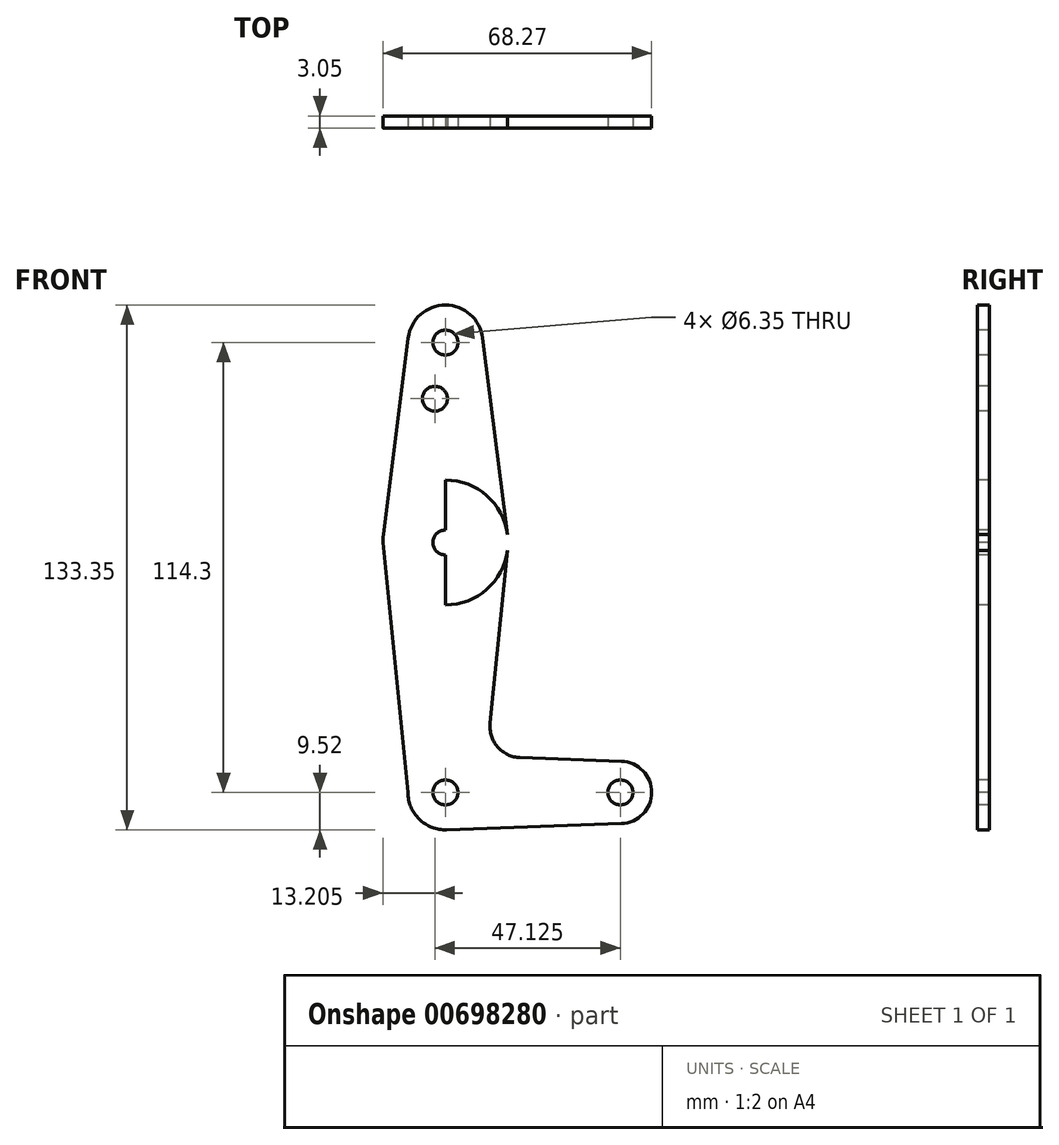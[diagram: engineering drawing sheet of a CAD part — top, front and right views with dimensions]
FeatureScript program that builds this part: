
annotation { "Feature Type Name" : "Feature", "Feature Type Description" : "" }
export const myFeature = defineFeature(function(context is Context, id is Id, definition is map)
    precondition{}
    {
        {
            var Q0;
            Q0=qCreatedBy(makeId("Front.planeOp"),FACE);
            var sketch = newSketch(context, id + "F0", { "sketchPlane" : qUnion([Q0])});
            skLineSegment(sketch, "E0", {"start": v(0, 114.3) * mm, "end": v(0, 0) * mm});
            skLineSegment(sketch, "E1", {"start": v(44.45, 0) * mm, "end": v(0, 0) * mm});
            skCircle(sketch, "E2", {"center": v(0, 114.3) * mm, "radius": 9.53 * mm});
            skCircle(sketch, "E3", {"center": v(0, 0) * mm, "radius": 9.53 * mm});
            skCircle(sketch, "E4", {"center": v(44.45, 0) * mm, "radius": 7.94 * mm});
            skCircle(sketch, "E5", {"center": v(0, 63.5) * mm, "radius": 15.88 * mm});
            skLineSegment(sketch, "E6", {"start": v(-9.45, 115.5) * mm, "end": v(-15.75, 65.48) * mm});
            skLineSegment(sketch, "E7", {"start": v(9.45, 115.5) * mm, "end": v(15.75, 65.48) * mm});
            skLineSegment(sketch, "E8", {"start": v(15.75, 61.52) * mm, "end": v(11.34, 17.6) * mm});
            skLineSegment(sketch, "E9", {"start": v(18.97, 8.85) * mm, "end": v(44.73, 7.93) * mm});
            skLineSegment(sketch, "E10", {"start": v(0.34, -9.52) * mm, "end": v(44.73, -7.93) * mm});
            skCircle(sketch, "E11", {"center": v(0, 114.3) * mm, "radius": 3.18 * mm});
            skCircle(sketch, "E12", {"center": v(0, 63.5) * mm, "radius": 3.18 * mm});
            skCircle(sketch, "E13", {"center": v(0, 0) * mm, "radius": 3.18 * mm});
            skCircle(sketch, "E14", {"center": v(44.45, 0) * mm, "radius": 3.18 * mm});
            skCircle(sketch, "E15", {"center": v(-2.68, 100.03) * mm, "radius": 3.18 * mm});
            skLineSegment(sketch, "E16", {"start": v(-15.88, 63.5) * mm, "end": v(-9.52, 0) * mm});
            skArc(sketch, "E17.filletArc", {"start": v(11.34, 17.6) * mm, "mid": v(13.26, 11.57) * mm, "end": v(18.97, 8.85) * mm});
            skSolve(sketch);
        }
        {
            var Q0;
            Q0=makeQuery(id+"F0.imprint","IMPRINT",FACE,{"disambiguationData":[TD([[makeQuery(id+"F0.imprint","IMPRINT",EDGE,{"derivedFrom":sQuery(id+"F0.wireOp",EDGE,"E11")}),-1.0]])]});
            var Q1;
            {var subQ0=sQuery(id+"F0.wireOp",EDGE,"E6");Q1=makeQuery(id+"F0.imprint","IMPRINT",FACE,{"disambiguationData":[TD([[makeQuery(id+"F0.imprint","IMPRINT",EDGE,{"derivedFrom":subQ0}),1.0]])]});}
            var Q2;
            {var subQ0=sQuery(id+"F0.wireOp",EDGE,"E7");Q2=makeQuery(id+"F0.imprint","IMPRINT",FACE,{"disambiguationData":[TD([[makeQuery(id+"F0.imprint","IMPRINT",EDGE,{"derivedFrom":subQ0}),-1.0]])]});}
            var Q3;
            {var subQ0=sQuery(id+"F0.wireOp",EDGE,"E5");var subQ2=sQuery(id+"F0.wireOp",EDGE,"E0");var subQ7=makeQuery(id+"F0.imprint","INTERSECT",VERTEX,{"disambiguationData":[OD(0.0)],"derivedFrom":[subQ2,subQ0]});Q3=makeQuery(id+"F0.imprint","IMPRINT",FACE,{"disambiguationData":[TD([[makeQuery(id+"F0.imprint","IMPRINT",EDGE,{"disambiguationData":[TD([[subQ7,-1.0]])],"derivedFrom":subQ2}),1.0]])]});}
            var Q4;
            {var subQ0=sQuery(id+"F0.wireOp",EDGE,"E5");var subQ5=sQuery(id+"F0.wireOp",EDGE,"E0");var subQ9=makeQuery(id+"F0.imprint","INTERSECT",VERTEX,{"disambiguationData":[OD(0.0)],"derivedFrom":[subQ5,subQ0]});Q4=makeQuery(id+"F0.imprint","IMPRINT",FACE,{"disambiguationData":[TD([[makeQuery(id+"F0.imprint","IMPRINT",EDGE,{"disambiguationData":[TD([[subQ9,-1.0]])],"derivedFrom":subQ5}),-1.0]])]});}
            var Q5;
            {var subQ0=sQuery(id+"F0.wireOp",EDGE,"E5");var subQ1=sQuery(id+"F0.wireOp",EDGE,"E0");var subQ2=makeQuery(id+"F0.imprint","INTERSECT",VERTEX,{"disambiguationData":[OD(1.0)],"derivedFrom":[subQ1,subQ0]});Q5=makeQuery(id+"F0.imprint","IMPRINT",FACE,{"disambiguationData":[TD([[makeQuery(id+"F0.imprint","IMPRINT",EDGE,{"disambiguationData":[TD([[subQ2,-1.0]])],"derivedFrom":subQ1}),-1.0]])]});}
            var Q6;
            {var subQ8=sQuery(id+"F0.wireOp",EDGE,"E8");Q6=makeQuery(id+"F0.imprint","IMPRINT",FACE,{"disambiguationData":[TD([[makeQuery(id+"F0.imprint","IMPRINT",EDGE,{"derivedFrom":subQ8}),-1.0]])]});}
            var Q7;
            {var subQ5=sQuery(id+"F0.wireOp",EDGE,"E10");Q7=makeQuery(id+"F0.imprint","IMPRINT",FACE,{"disambiguationData":[TD([[makeQuery(id+"F0.imprint","IMPRINT",EDGE,{"derivedFrom":subQ5}),1.0]])]});}
            var Q8;
            {var subQ0=sQuery(id+"F0.wireOp",EDGE,"E3");var subQ2=sQuery(id+"F0.wireOp",EDGE,"E0");var subQ3=makeQuery(id+"F0.imprint","INTERSECT",VERTEX,{"derivedFrom":[subQ2,subQ0]});Q8=makeQuery(id+"F0.imprint","IMPRINT",FACE,{"disambiguationData":[TD([[makeQuery(id+"F0.imprint","IMPRINT",EDGE,{"disambiguationData":[TD([[subQ3,-1.0]])],"derivedFrom":subQ2}),-1.0]])]});}
            var Q9;
            Q9=makeQuery(id+"F0.imprint","IMPRINT",FACE,{"disambiguationData":[TD([[makeQuery(id+"F0.imprint","IMPRINT",EDGE,{"derivedFrom":sQuery(id+"F0.wireOp",EDGE,"E14")}),-1.0]])]});
            var Q10;
            {var subQ0=sQuery(id+"F0.wireOp",EDGE,"E3");var subQ1=sQuery(id+"F0.wireOp",EDGE,"E0");var subQ2=makeQuery(id+"F0.imprint","INTERSECT",VERTEX,{"derivedFrom":[subQ1,subQ0]});Q10=makeQuery(id+"F0.imprint","IMPRINT",FACE,{"disambiguationData":[TD([[makeQuery(id+"F0.imprint","IMPRINT",EDGE,{"disambiguationData":[TD([[subQ2,-1.0]])],"derivedFrom":subQ1}),1.0]])]});}
            extrude(context, id + "F1", {"entities" : qUnion([Q0, Q1, Q2, Q3, Q4, Q5, Q6, Q7, Q8, Q9, Q10]), "surfaceOperationType" : NewSurfaceOperationType.ADD, "oppositeDirection" : true, "depth" : 3.05 * mm, "offsetDistance" : 25.4 * mm});
        }
    });
